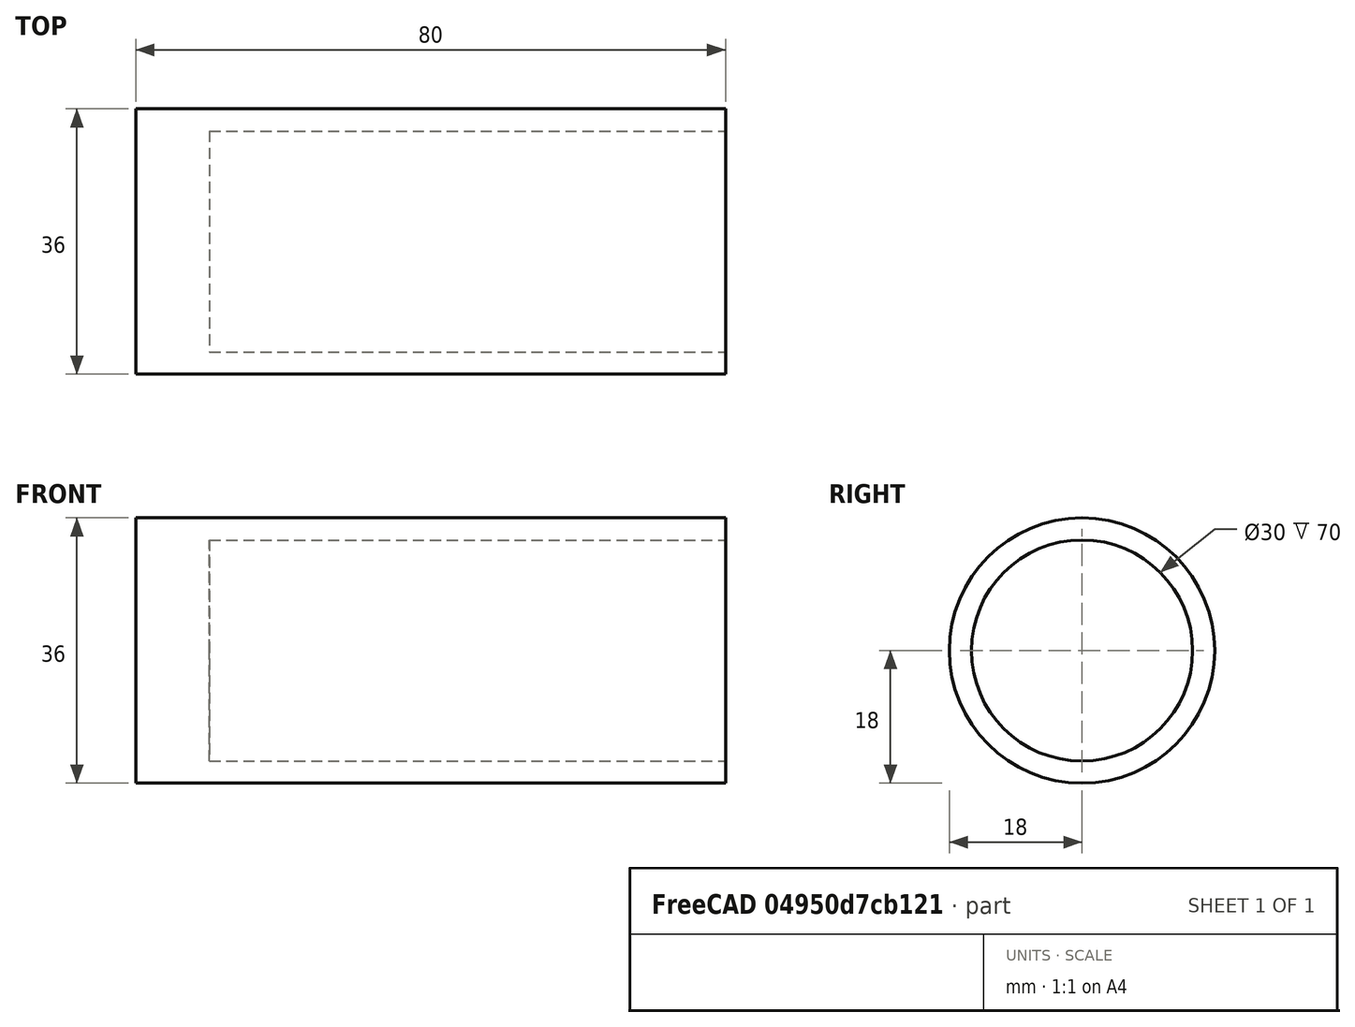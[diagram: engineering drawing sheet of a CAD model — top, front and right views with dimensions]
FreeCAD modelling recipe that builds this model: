
FCSTD DOCUMENT  (FreeCAD 0.19R)
Label: cap
License: All rights reserved
LicenseURL: http://en.wikipedia.org/wiki/All_rights_reserved
objects: Sketcher::SketchObject×1, PartDesign::Revolution×1, PartDesign::Body×1
note: 4 computed .brp shape members not serialized (recipe doc carries the construction recipe); baked Part::Feature solids carry a one-line shape summary decoded from their .brp

FEATURE [Sketcher::SketchObject] Sketch
  MapMode = 5
  Support = -> [XY_Plane]
  sketch-geometry (6):
    g0: LineSegment StartX=0 StartY=18 StartZ=0 EndX=80 EndY=18 EndZ=0
    g1: LineSegment StartX=10 StartY=15 StartZ=0 EndX=80 EndY=15 EndZ=0
    g2: LineSegment StartX=80 StartY=18 StartZ=0 EndX=80 EndY=15 EndZ=0
    g3: LineSegment StartX=0 StartY=0 StartZ=0 EndX=0 EndY=18 EndZ=0
    g4: LineSegment StartX=10 StartY=15 StartZ=0 EndX=10 EndY=0 EndZ=0
    g5: LineSegment StartX=0 StartY=0 StartZ=0 EndX=10 EndY=0 EndZ=0
  constraints (17):
    c: Horizontal(g0)
    c: Horizontal(g1)
    c: Coincident(g2,g0)
    c: Coincident(g2,g1)
    c: Vertical(g2)
    c: DistanceX(g-1,g1) = 80
    c: Coincident(g3,g-1)
    c: Coincident(g3,g0)
    c: Coincident(g4,g1)
    c: PointOnObject(g4,g-1)
    c: Coincident(g5,g3)
    c: Coincident(g5,g4)
    c: Parallel(g3,g4)
    c: Distance(g1,g3) = 10
    c: DistanceY(g2,g2) = 3
    c: Distance(g4,g1) = 15
    c: Vertical(g3)
FEATURE [PartDesign::Revolution] Revolution
  AllowMultiFace = false
  Angle = 360
  Axis = (1,0,0)
  Base = (0,0,0)
  Profile = -> Sketch
  ReferenceAxis = -> X_Axis
FEATURE [PartDesign::Body] Body
  Group = -> [Sketch,Revolution]
  Origin = -> Origin
  Tip = -> Revolution
